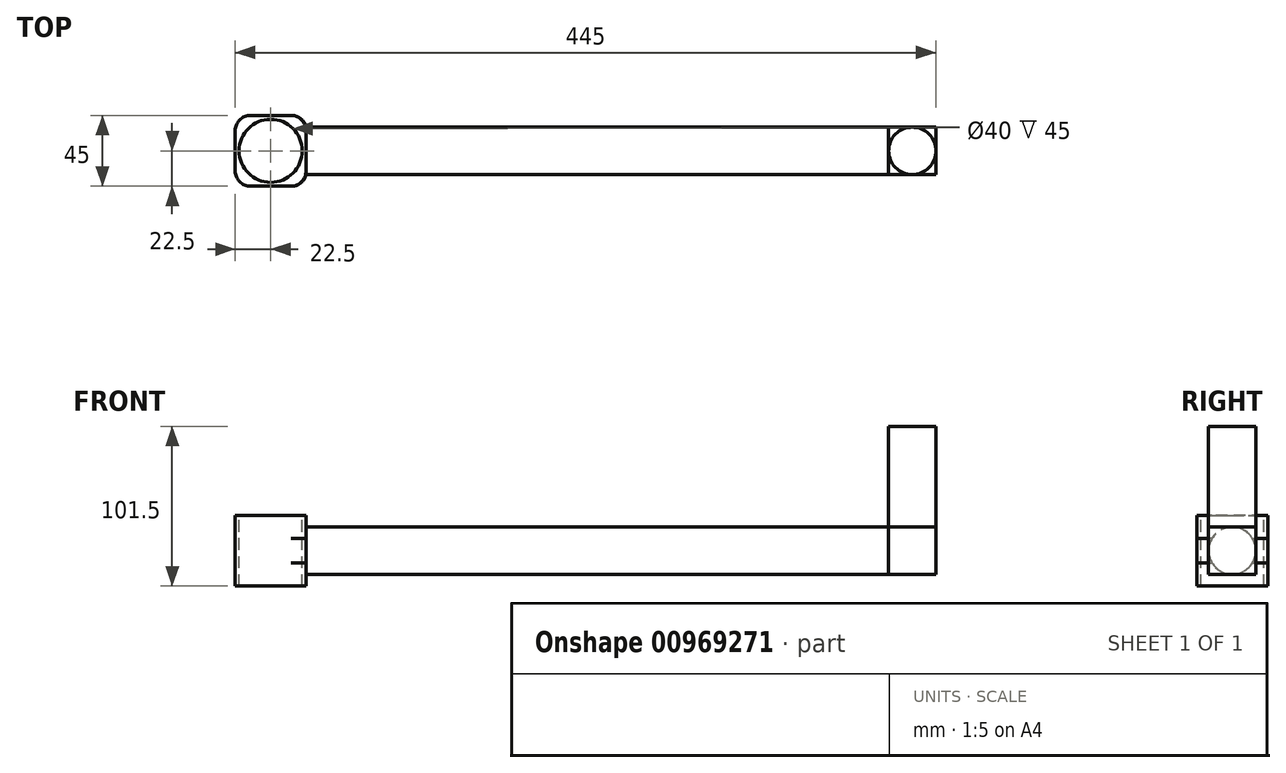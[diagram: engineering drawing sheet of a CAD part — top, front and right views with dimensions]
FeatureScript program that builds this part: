
annotation { "Feature Type Name" : "Feature", "Feature Type Description" : "" }
export const myFeature = defineFeature(function(context is Context, id is Id, definition is map)
    precondition{}
    {
        {
            var Q0;
            Q0=qCreatedBy(makeId("Right.planeOp"),FACE);
            var sketch = newSketch(context, id + "F0", { "sketchPlane" : qUnion([Q0])});
            skCircle(sketch, "E0", {"center": v(0, 0) * mm, "radius": 15 * mm});
            skSolve(sketch);
        }
        {
            var Q0;
            Q0 = qSketchRegion(id + "F0", true);
            var Q1;
            Q1=makeQuery(id+"F0.imprint","IMPRINT",FACE,{"disambiguationData":[TD([[makeQuery(id+"F0.imprint","IMPRINT",EDGE,{"derivedFrom":sQuery(id+"F0.wireOp",EDGE,"E0")}),1.0]])]});
            extrude(context, id + "F1", {"entities" : qUnion([Q0, Q1]), "depth" : 370 * mm, "offsetDistance" : 25 * mm});
        }
        {
            var Q0;
            Q0=makeQuery(id+"F1.opExtrude","CAP_FACE",FACE,{"disambiguationData":[OSD([sQuery(id+"F0.wireOp",EDGE,"E0")])],"isStart":false});
            var sketch = newSketch(context, id + "F2", { "sketchPlane" : qUnion([Q0])});
            skCircle(sketch, "E1.0", {"center": v(0, 0) * mm, "radius": 15 * mm, "construction": true});
            skLineSegment(sketch, "E2", {"start": v(0, 0) * mm, "end": v(15, 0) * mm, "construction": true});
            skLineSegment(sketch, "E3", {"start": v(15, 0) * mm, "end": v(15, 15) * mm, "construction": true});
            skLineSegment(sketch, "E4.bottom", {"start": v(15, 15) * mm, "end": v(-15, 15) * mm});
            skLineSegment(sketch, "E4.top", {"start": v(15, -15) * mm, "end": v(-15, -15) * mm});
            skLineSegment(sketch, "E4.left", {"start": v(15, 15) * mm, "end": v(15, -15) * mm});
            skLineSegment(sketch, "E4.right", {"start": v(-15, 15) * mm, "end": v(-15, -15) * mm});
            skSolve(sketch);
        }
        {
            var Q0;
            {var subQ0=sQuery(id+"F2.wireOp",EDGE,"E4.right");var subQ1=sQuery(id+"F2.wireOp",EDGE,"E4.bottom");var subQ2=makeQuery(id+"F2.imprint","INTERSECT",VERTEX,{"derivedFrom":[subQ1,subQ0]});Q0=makeQuery(id+"F2.imprint","IMPRINT",FACE,{"disambiguationData":[TD([[makeQuery(id+"F2.imprint","IMPRINT",EDGE,{"disambiguationData":[TD([[subQ2,1.0]])],"derivedFrom":subQ1}),1.0]])]});}
            var Q1;
            {var subQ0=sQuery(id+"F2.wireOp",EDGE,"E4.left");var subQ1=sQuery(id+"F2.wireOp",EDGE,"E4.bottom");var subQ2=makeQuery(id+"F2.imprint","INTERSECT",VERTEX,{"derivedFrom":[subQ1,subQ0]});Q1=makeQuery(id+"F2.imprint","IMPRINT",FACE,{"disambiguationData":[TD([[makeQuery(id+"F2.imprint","IMPRINT",EDGE,{"disambiguationData":[TD([[subQ2,-1.0]])],"derivedFrom":subQ1}),1.0]])]});}
            var Q2;
            {var subQ0=sQuery(id+"F2.wireOp",EDGE,"E4.right");var subQ1=sQuery(id+"F2.wireOp",EDGE,"E4.top");var subQ2=makeQuery(id+"F2.imprint","INTERSECT",VERTEX,{"derivedFrom":[subQ1,subQ0]});Q2=makeQuery(id+"F2.imprint","IMPRINT",FACE,{"disambiguationData":[TD([[makeQuery(id+"F2.imprint","IMPRINT",EDGE,{"disambiguationData":[TD([[subQ2,1.0]])],"derivedFrom":subQ1}),-1.0]])]});}
            var Q3;
            {var subQ0=makeQuery(id+"F1.opExtrude","CAP_EDGE",EDGE,{"disambiguationData":[OSD([sQuery(id+"F0.wireOp",EDGE,"E0")])],"isStart":false});var subQ1=makeQuery(id+"F2.imprint","INTERSECT",VERTEX,{"derivedFrom":[subQ0,sQuery(id+"F2.wireOp",EDGE,"E4.bottom")]});Q3=makeQuery(id+"F2.imprint","IMPRINT",FACE,{"disambiguationData":[TD([[makeQuery(id+"F2.imprint","IMPRINT",EDGE,{"disambiguationData":[TD([[subQ1,1.0]])],"derivedFrom":subQ0}),1.0]])]});}
            var Q4;
            {var subQ0=sQuery(id+"F2.wireOp",EDGE,"E4.left");var subQ1=sQuery(id+"F2.wireOp",EDGE,"E4.top");var subQ2=makeQuery(id+"F2.imprint","INTERSECT",VERTEX,{"derivedFrom":[subQ1,subQ0]});Q4=makeQuery(id+"F2.imprint","IMPRINT",FACE,{"disambiguationData":[TD([[makeQuery(id+"F2.imprint","IMPRINT",EDGE,{"disambiguationData":[TD([[subQ2,-1.0]])],"derivedFrom":subQ1}),-1.0]])]});}
            extrude(context, id + "F3", {"entities" : qUnion([Q0, Q1, Q2, Q3, Q4]), "operationType" : NewBodyOperationType.ADD, "depth" : 30 * mm, "offsetDistance" : 25 * mm});
        }
        {
            var Q0;
            Q0=makeQuery(id+"F3.opExtrude","SWEPT_FACE",FACE,{"disambiguationData":[OSD([sQuery(id+"F2.wireOp",EDGE,"E4.bottom")])]});
            var sketch = newSketch(context, id + "F4", { "sketchPlane" : qUnion([Q0])});
            skLineSegment(sketch, "E5", {"start": v(370, 15) * mm, "end": v(400, -15) * mm, "construction": true});
            skLineSegment(sketch, "E6", {"start": v(400, 15) * mm, "end": v(370, -15) * mm, "construction": true});
            skCircle(sketch, "E7", {"center": v(385, 0) * mm, "radius": 15 * mm});
            skSolve(sketch);
        }
        {
            var Q0;
            {var subQ0=sQuery(id+"F4.wireOp",EDGE,"E7");var subQ2=sQuery(id+"F2.wireOp",EDGE,"E4.bottom");var subQ4=makeQuery(id+"F4.imprint","INTERSECT",VERTEX,{"derivedFrom":[makeQuery(id+"F3.opExtrude","CAP_EDGE",EDGE,{"disambiguationData":[OSD([subQ2])],"isStart":false}),subQ0]});Q0=makeQuery(id+"F4.imprint","IMPRINT",FACE,{"disambiguationData":[TD([[makeQuery(id+"F4.imprint","IMPRINT",EDGE,{"disambiguationData":[TD([[subQ4,-1.0]])],"derivedFrom":subQ0}),1.0]])]});}
            extrude(context, id + "F5", {"entities" : qUnion([Q0]), "operationType" : NewBodyOperationType.ADD, "depth" : 64 * mm, "offsetDistance" : 25 * mm});
        }
        {
            var Q0;
            Q0=makeQuery(id+"F1.opExtrude","CAP_FACE",FACE,{"disambiguationData":[OSD([sQuery(id+"F0.wireOp",EDGE,"E0")])],"isStart":true});
            var sketch = newSketch(context, id + "F6", { "sketchPlane" : qUnion([Q0])});
            skLineSegment(sketch, "E8.bottom", {"start": v(22.5, 22.5) * mm, "end": v(-22.5, 22.5) * mm});
            skLineSegment(sketch, "E8.top", {"start": v(22.5, -22.5) * mm, "end": v(-22.5, -22.5) * mm});
            skLineSegment(sketch, "E8.left", {"start": v(22.5, 22.5) * mm, "end": v(22.5, -22.5) * mm});
            skLineSegment(sketch, "E8.right", {"start": v(-22.5, 22.5) * mm, "end": v(-22.5, -22.5) * mm});
            skPoint(sketch, "E8.middle", {"position": v(0, 0) * mm});
            skSolve(sketch);
        }
        {
            var Q0;
            Q0=makeQuery(id+"F6.imprint","IMPRINT",FACE,{"disambiguationData":[TD([[makeQuery(id+"F6.imprint","IMPRINT",EDGE,{"derivedFrom":sQuery(id+"F6.wireOp",EDGE,"E8.bottom")}),1.0]])]});
            var Q1;
            Q1=makeQuery(id+"F6.imprint","IMPRINT",FACE,{"disambiguationData":[TD([[makeQuery(id+"F6.imprint","IMPRINT",EDGE,{"derivedFrom":makeQuery(id+"F1.opExtrude","CAP_EDGE",EDGE,{"disambiguationData":[OSD([sQuery(id+"F0.wireOp",EDGE,"E0")])],"isStart":true})}),-1.0]])]});
            extrude(context, id + "F7", {"entities" : qUnion([Q0, Q1]), "operationType" : NewBodyOperationType.ADD, "depth" : 45 * mm, "offsetDistance" : 25 * mm});
        }
        {
            var Q0;
            Q0=makeQuery(id+"F7.opExtrude","SWEPT_FACE",FACE,{"disambiguationData":[OSD([sQuery(id+"F6.wireOp",EDGE,"E8.bottom")])]});
            var sketch = newSketch(context, id + "F8", { "sketchPlane" : qUnion([Q0])});
            skLineSegment(sketch, "E9", {"start": v(-45, 22.5) * mm, "end": v(0, -22.5) * mm, "construction": true});
            skLineSegment(sketch, "E10", {"start": v(0, 22.5) * mm, "end": v(-45, -22.5) * mm, "construction": true});
            skCircle(sketch, "E11", {"center": v(-22.5, 0) * mm, "radius": 20 * mm});
            skSolve(sketch);
        }
        {
            var Q0;
            Q0=makeQuery(id+"F8.imprint","IMPRINT",FACE,{"disambiguationData":[TD([[makeQuery(id+"F8.imprint","IMPRINT",EDGE,{"derivedFrom":sQuery(id+"F8.wireOp",EDGE,"E11")}),1.0]])]});
            extrude(context, id + "F9", {"entities" : qUnion([Q0]), "operationType" : NewBodyOperationType.REMOVE, "endBound" : BoundingType.UP_TO_NEXT, "oppositeDirection" : true, "depth" : 25 * mm, "offsetDistance" : 25 * mm});
        }
        {
            var Q0;
            Q0=makeQuery(id+"F7.opExtrude","CAP_EDGE",EDGE,{"disambiguationData":[OSD([sQuery(id+"F6.wireOp",EDGE,"E8.left")])],"isStart":true});
            var Q1;
            Q1=makeQuery(id+"F7.opExtrude","CAP_EDGE",EDGE,{"disambiguationData":[OSD([sQuery(id+"F6.wireOp",EDGE,"E8.left")])],"isStart":false});
            var Q2;
            Q2=makeQuery(id+"F7.opExtrude","CAP_EDGE",EDGE,{"disambiguationData":[OSD([sQuery(id+"F6.wireOp",EDGE,"E8.right")])],"isStart":false});
            var Q3;
            Q3=makeQuery(id+"F7.opExtrude","CAP_EDGE",EDGE,{"disambiguationData":[OSD([sQuery(id+"F6.wireOp",EDGE,"E8.right")])],"isStart":true});
            fillet(context, id + "F10", {"entities" : qUnion([Q0, Q1, Q2, Q3]), "radius" : 9.66 * mm, "tangentPropagation" : true, "allowEdgeOverflow" : false});
        }
    });
